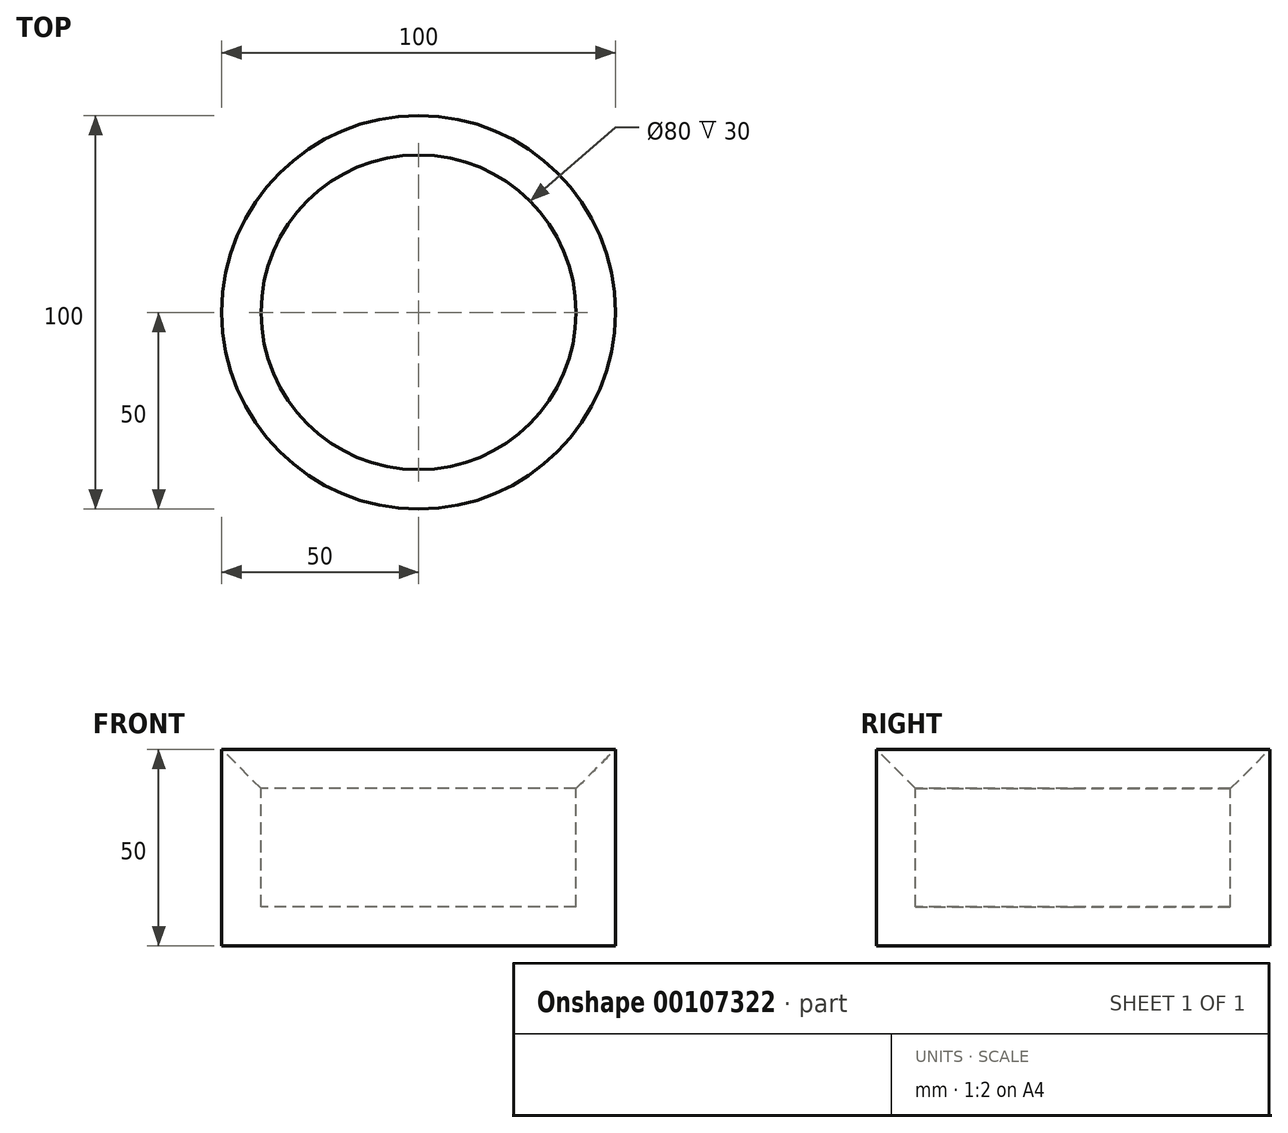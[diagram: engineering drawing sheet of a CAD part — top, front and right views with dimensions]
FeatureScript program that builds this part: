
annotation { "Feature Type Name" : "Feature", "Feature Type Description" : "" }
export const myFeature = defineFeature(function(context is Context, id is Id, definition is map)
    precondition{}
    {
        {
            var Q0;
            Q0=qCreatedBy(makeId("Front.planeOp"),FACE);
            var sketch = newSketch(context, id + "F0", { "sketchPlane" : qUnion([Q0])});
            skLineSegment(sketch, "E0", {"start": v(0, 0) * mm, "end": v(-50, 0) * mm});
            skLineSegment(sketch, "E1", {"start": v(-50, 0) * mm, "end": v(-50, 50) * mm});
            skLineSegment(sketch, "E2", {"start": v(-50, 50) * mm, "end": v(-40, 40) * mm});
            skLineSegment(sketch, "E3", {"start": v(-40, 40) * mm, "end": v(-40, 10) * mm});
            skLineSegment(sketch, "E4", {"start": v(-40, 10) * mm, "end": v(0, 10) * mm});
            skLineSegment(sketch, "E5", {"start": v(0, 10) * mm, "end": v(0, 0) * mm});
            skSolve(sketch);
        }
        {
            var Q0;
            Q0 = qSketchRegion(id + "F0", true);
            var Q1;
            Q1=sQuery(id+"F0.wireOp",EDGE,"E5");
            revolve(context, id + "F1", {"entities" : qUnion([Q0]), "axis" : qUnion([Q1]), "revolveType" : RevolveType.FULL});
        }
    });
